# Revit family: Faucet-Lavatory-Spout-KOHLER-COMPONENTS-K-77965T_1
name_source: partatom
category: Plumbing Fixtures
revit_build: Autodesk Revit 2017 (Build: 20160225_1515(x64)
units: mm (PartAtom-declared; Revit-internal decimal feet)

## family parameters
Cut with Voids When Loaded = No
Host = Face
OmniClass Number = 23.31.11.00
OmniClass Title = Faucets
Part Type = Normal
Room Calculation Point = No
Round Connector Dimension = Use Diameter
Shared = No

## types (6) — shared parameters
ADA Compliant = No
Assembly Code = D2010
CW Connection = No
Cold Water Inlet = Cold Water Inlet
Date Modified = 06/09/2020
Default Elevation = 36"
Description = 8-inch washbasin faucet with curved tube-shaped spout
Drain Included = Yes
Flow Rate = 0 GPM
HW Connection = No
Height = 14 7/16"
Hot Water Inlet = Hot Water Inlet
Length = 6 5/8"
Manufacturer = KOHLER Co.
Master Format 2014 = 22 41 39
Master Format 2014 Name = Residential Faucets, Supplies, and Trim
Material = Premium Metal Construction
Pressure = 0.00 psi
Product Documentation Link = http://files.kohler.com.cn
Product Name = COMPONENTS
Product Page URL = http://www.kohler.com.cn
Spout Reach = 6 5/8"
URL = http://www.kohler.com.cn
Vent Connection = No
Waste Connection = No
Waste Water Outlet = Waste Water Outlet
WaterSense Certified = No
Width = 2 3/8"

## per-type parameters (varying)
| type | Finish | Model | Type |
| CP-Polished Chrome | Kohler-Metal-CP-Polished_Chrome | K-77965T-CP | 1 |
| BN-Roman silver | Kohler-Metal-BN-Roman_Silver | K-77965T-BN | 2 |
| RGD-Rose Gold | Kohler-Metal-RGD-Rose_Gold | K-77965T-RGD | 3 |
| AF-Flange Gold | Kohler-Metal-AF-Flange_Gold | K-77965T-AF | 4 |
| 2BL-Original Black | Kohler-Metal-2BL-Original_Black | K-77965T-2BL | 5 |
| TT-Titanium Silver | Kohler-Metal-TT-Titanium_Silver | K-77965T-TT | 6 |

## geometry (parser evidence)
native form markers: Sweep x5
no freeform markers — native parametric forms only
